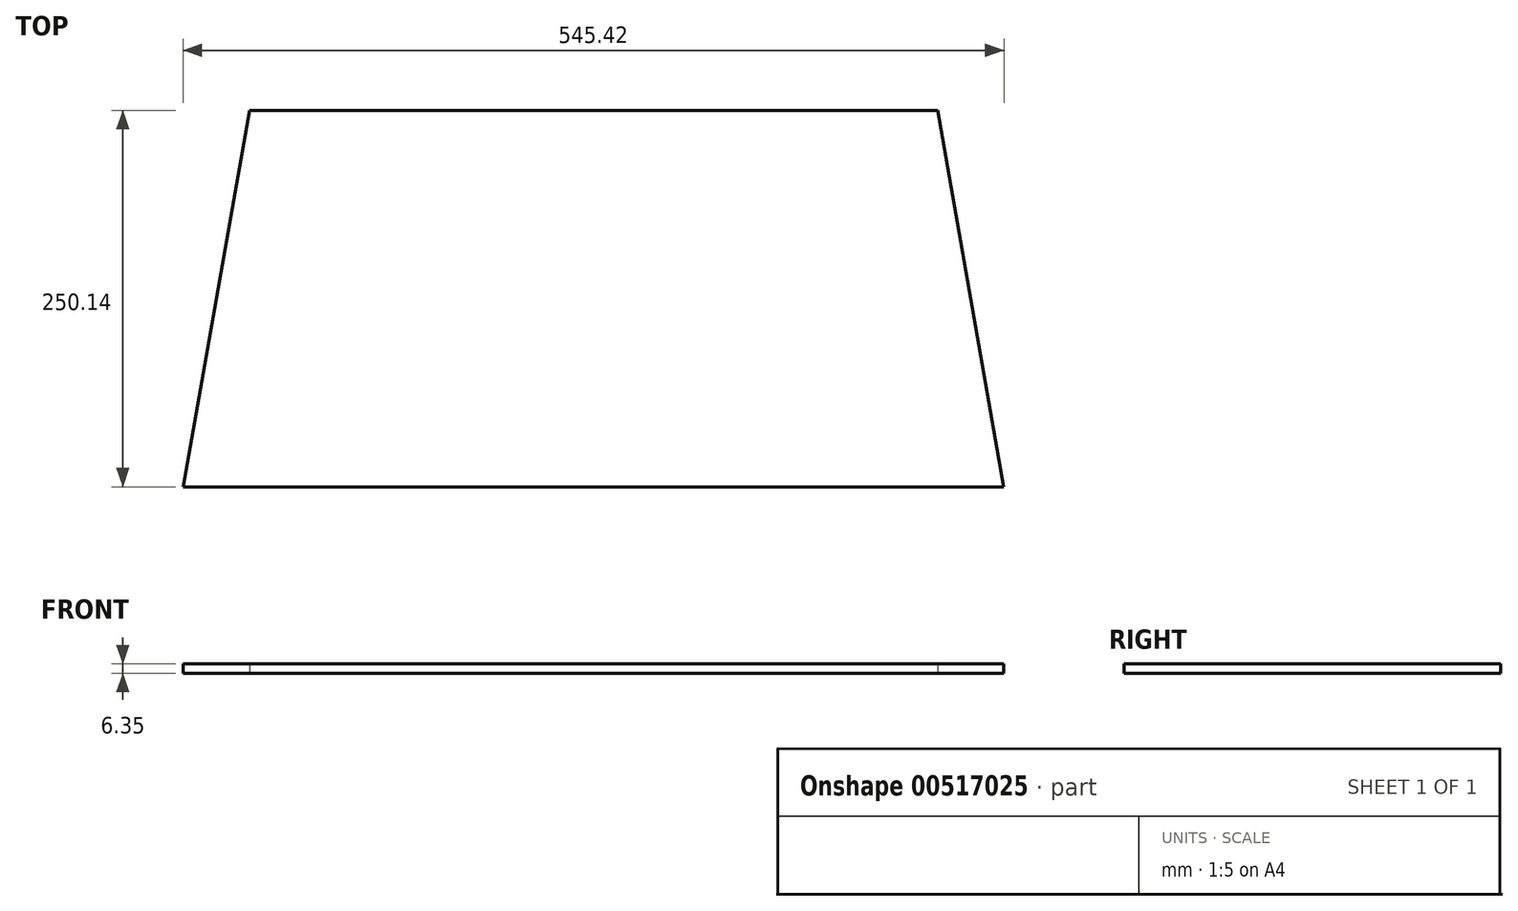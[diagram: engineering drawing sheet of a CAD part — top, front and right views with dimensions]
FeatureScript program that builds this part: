
annotation { "Feature Type Name" : "Feature", "Feature Type Description" : "" }
export const myFeature = defineFeature(function(context is Context, id is Id, definition is map)
    precondition{}
    {
        {
            var Q0;
            Q0=qCreatedBy(makeId("Top.planeOp"),FACE);
            var sketch = newSketch(context, id + "F0", { "sketchPlane" : qUnion([Q0])});
            skLineSegment(sketch, "E0.bottom", {"start": v(-275.22, 85.06) * mm, "end": v(181.98, 85.06) * mm});
            skLineSegment(sketch, "E1", {"start": v(-275.22, 85.06) * mm, "end": v(-319.33, -165.08) * mm});
            skLineSegment(sketch, "E2", {"start": v(181.98, 85.06) * mm, "end": v(226.09, -165.08) * mm});
            skLineSegment(sketch, "E3", {"start": v(-319.33, -165.08) * mm, "end": v(226.09, -165.08) * mm});
            skSolve(sketch);
        }
        {
            var Q0;
            Q0=makeQuery(id+"F0.imprint","IMPRINT",FACE,{"disambiguationData":[TD([[makeQuery(id+"F0.imprint","IMPRINT",EDGE,{"derivedFrom":sQuery(id+"F0.wireOp",EDGE,"E0.bottom")}),-1.0]])]});
            extrude(context, id + "F1", {"entities" : qUnion([Q0]), "depth" : 12.7 * mm, "offsetDistance" : 25.4 * mm});
        }
        {
            var Q0;
            Q0=makeQuery(id+"F1.opExtrude","CAP_FACE",FACE,{"disambiguationData":[OSD([sQuery(id+"F0.wireOp",EDGE,"E0.bottom"),sQuery(id+"F0.wireOp",EDGE,"E1"),sQuery(id+"F0.wireOp",EDGE,"E2"),sQuery(id+"F0.wireOp",EDGE,"E3")])],"isStart":false});
            extrude(context, id + "F2", {"entities" : qUnion([Q0]), "operationType" : NewBodyOperationType.REMOVE, "oppositeDirection" : true, "depth" : 6.35 * mm, "offsetDistance" : 25.4 * mm});
        }
    });
